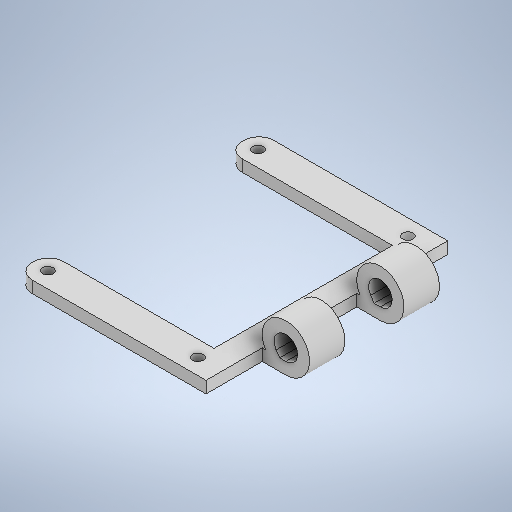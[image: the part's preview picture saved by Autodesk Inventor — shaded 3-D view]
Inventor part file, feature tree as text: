
AUTODESK INVENTOR PART (.ipt)
format: ipt  version: 2025.1 (Build 291241020, 241B)  size: 353,280 bytes
history: native  units: mm
features: extrude x3, sketch x3, sweep x1, plane x1, fillet x1, hole x1, mirror x1, projected_geometry x1
ambient origin geometry x8: Origin, YZ Plane, XZ Plane, XY Plane, X Axis, Y Axis, Z Axis, Center Point
bodies: Solid1 (feature_tree)
feature tree (12):
  extrude  "Extrusion1"  Depth=102.3mm
  sweep  "Sweep1"
  extrude  "Extrusion2"  TaperAngle=0.0deg  [1 undecoded]
  extrude  "Extrusion4"  Depth=6.35mm
  plane  "Work Plane2"
  fillet  "Fillet1"  [1 undecoded]
  hole  "Hole2"  [1 undecoded]
  mirror  "Mirror4"
  projected_geometry  "Projected Loop1"
  sketch  "Sketch3"  dims[d0=80.0mm d1=102.3mm]
  sketch  "Sketch8"  dims[d2=5.0mm d3=0.0mm d4=10.0mm]
  sketch  "Sketch11"  dims[d5=10.0mm d7=0.0mm d8=0.0mm d10=7.0mm d13=0.0mm d14=0.0mm d46=15.0mm d48=19.319mm d49=0.0mm d50=25.0mm d51=15.0mm d52=23.5mm d62=13.4mm d63=13.4mm d64=10.0mm d65=6.35mm d74=63.5mm d77=6.35mm d79=4.5mm d80=6.0mm d81=9.4mm d82=2.0mm d83=90.0deg d84=8.0mm d85=20.594885mm d43=0.5mm d44=0.872665mm d45=0.5mm]
note: 3 required parameter values undecoded (feature->parameter linkage not recoverable at this tier; creation-order binding heuristic only, values carry confidence <= 0.55)
